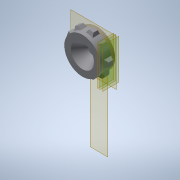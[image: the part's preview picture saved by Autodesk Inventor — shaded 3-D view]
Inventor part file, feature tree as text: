
AUTODESK INVENTOR PART (.ipt)
format: ipt  version: 2020 (Build 240168000, 168)  size: 204,288 bytes
history: native  units: mm
features: other x12, sketch x6, extrude x4, loft x1, pattern_circular x1, chamfer x1, reference x1
ambient origin geometry x8: Origin, YZ Plane, XZ Plane, XY Plane, X Axis, Y Axis, Z Axis, Center Point
bodies: Body1 (feature_tree)
feature tree (26):
  other  "Bryła1"
  other  "Płaszczyzna konstrukcyjna1"
  extrude  "Wyciągnięcie proste1"  Depth=20.0mm
  other  "Płaszczyzna konstrukcyjna2"
  extrude  "Wyciągnięcie proste2"  Depth=50.0mm
  extrude  "Wyciągnięcie proste3"  Depth=20.0mm TaperAngle=0.0deg
  other  "Płaszczyzna konstrukcyjna4"
  other  "Płaszczyzna konstrukcyjna5"
  sketch  "Szkic5"
  other  "Płaszczyzna konstrukcyjna6"
  loft  "Wyciągnięcie złożone1"
  pattern_circular  "Szyk kołowy1"  [2 undecoded]
  extrude  "Wyciągnięcie proste4"  TaperAngle=0.0deg  [1 undecoded]
  chamfer  "Faza2"  Distance=3.0mm
  sketch  "Szkic1"
  reference  "Odniesienie1"
  sketch  "Szkic3"
  sketch  "Szkic4"
  other  "Płaszczyzna konstrukcyjna3"
  sketch  "Szkic6"
  sketch  "Szkic7"
  other  "<userpath>\Desktop\3d\scanning-robot\Assembly1.iam"
  other  "Assembly1.iam"
  other  "Tower Pro MG90S Micro servo:2"
  other  "Крышка корпуса:1"
  other  "base:1"
note: 3 required parameter values undecoded (feature->parameter linkage not recoverable at this tier; creation-order binding heuristic only, values carry confidence <= 0.55)
